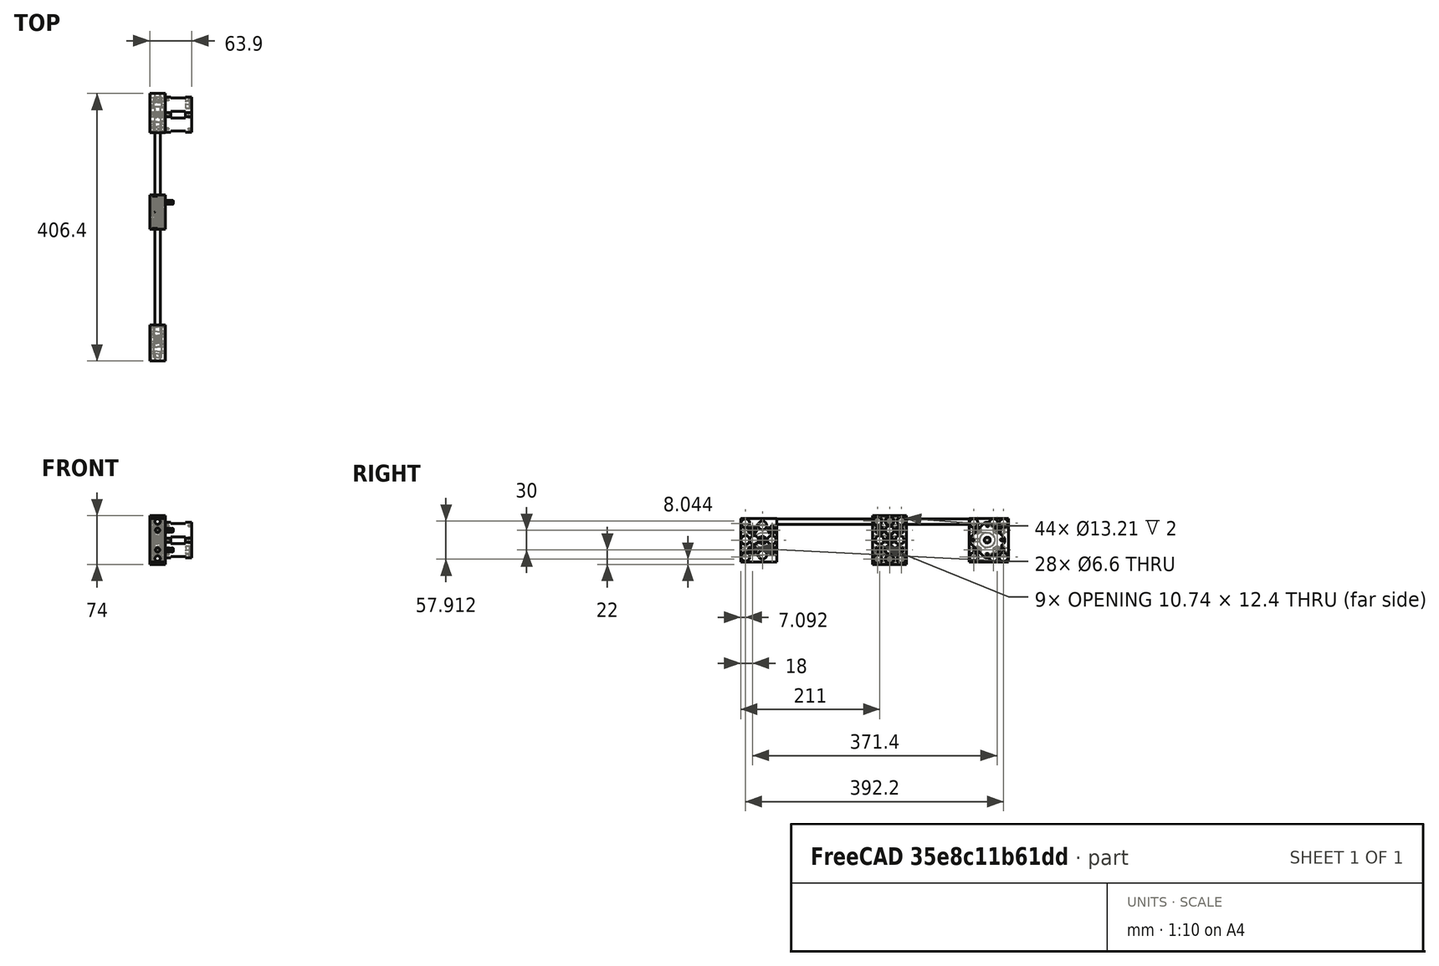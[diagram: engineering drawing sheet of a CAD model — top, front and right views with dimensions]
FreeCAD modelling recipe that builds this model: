
FCSTD DOCUMENT  (FreeCAD 0.16R6707 (Git))
Label: D3D Left Y Axis Simple
License: CreativeCommons Attribution
LicenseURL: http://creativecommons.org/licenses/by/4.0/
objects: Part::FeaturePython×7, Part::Feature×7, App::FeaturePython×4, Part::Mirroring×3, Part::MultiFuse×3, Part::Cylinder×1, App::DocumentObjectGroup×1
note: 21 computed .brp shape members not serialized (recipe doc carries the construction recipe); baked Part::Feature solids carry a one-line shape summary decoded from their .brp

FEATURE [Part::FeaturePython] Universal_axis_idler_side_01  # a2plus imported part (geometry in sourceFile) (typed FeaturePython)
  Placement = pos=(0,0,0) rot=(0.57735,0.57735,0.57735;2.0944rad)
  fixedPosition = true
  sourceFile = <userpath>/Downloads/Freecad/D3D Printer/Universal_axis_idler_side.fcstd
  timeLastImport = 1.48765e+09
  updateColors = true
FEATURE [Part::Mirroring] Part__Mirroring  label="Universal_axis_idler_side_01 (Mirror #1)"
  Base = (0,0,0)
  Normal = (1,0,0)
  Source = -> Universal_axis_idler_side_01
FEATURE [Part::MultiFuse] Fusion  label="Y1 Universal Axis Idler"
  Placement = pos=(12,33,33) rot=(0,0,1;0rad)
  Shapes = -> [Part__Mirroring,Universal_axis_idler_side_01]
FEATURE [Part::Cylinder] Cylinder  label="Rod"
  Angle = 360
  Height = 406.4
  Placement = pos=(12,9.155e-07,4.99999) rot=(0,0.707107,0.707107;3.14159rad)
  Radius = 3.96875
FEATURE [Part::FeaturePython] Clone006  label="Clone of Rod"  # Draft clone (typed FeaturePython)
  Objects = -> [Cylinder]
  Placement = pos=(11.9844,9.155e-07,61) rot=(-1,0,0;1.5708rad)
  Scale = (1,1,1)
FEATURE [Part::FeaturePython] Universal_axis_motor_side_01  # a2plus imported part (geometry in sourceFile) (typed FeaturePython)
  fixedPosition = false
  sourceFile = <userpath>/Downloads/Freecad/D3D Printer/Universal_axis_motor_side.fcstd
  timeLastImport = 1.48765e+09
  updateColors = true
FEATURE [Part::Mirroring] Part__Mirroring003  label="Universal_axis_motor_side_01 (Mirror #3)"
  Base = (0,0,0)
  Normal = (0,0,1)
  Source = -> Universal_axis_motor_side_01
FEATURE [Part::MultiFuse] Fusion005  label="Y1 Universal Axis Motor"
  Placement = pos=(12,374.4,33) rot=(0.57735,-0.57735,-0.57735;2.0944rad)
  Shapes = -> [Part__Mirroring003,Universal_axis_motor_side_01]
FEATURE [App::FeaturePython] planeConstraint01  label="Rods"  # a2plus constraint (typed FeaturePython)
  Object1 = Fusion005
  Object2 = Cylinder
  SubElement1 = Face3
  SubElement2 = Face2
  Type = plane
  directionConstraint = 0
  offset = 0
FEATURE [App::FeaturePython] planeConstraint02  label="Rods / Axis Motor "  # a2plus constraint (typed FeaturePython)
  Object1 = Fusion005
  Object2 = Clone006
  SubElement1 = Face42
  SubElement2 = Face2
  Type = plane
  directionConstraint = 0
  offset = 0
FEATURE [App::FeaturePython] planeConstraint03  label="Rods / Axis Idler"  # a2plus constraint (typed FeaturePython)
  Object1 = Fusion
  Object2 = Cylinder
  SubElement1 = Face3
  SubElement2 = Face3
  Type = plane
  directionConstraint = 1
  offset = 0
FEATURE [Part::FeaturePython] carriage_8mm_rods_01  # a2plus imported part (geometry in sourceFile) (typed FeaturePython)
  Placement = pos=(12.5,0,0) rot=(0,0,1;0rad)
  fixedPosition = false
  sourceFile = <userpath>/Downloads/Freecad/D3D Printer/Mess Stuff/axis_8mm STL + FCSTD/carriage_8mm_rods.FCStd
  timeLastImport = 1.48802e+09
  updateColors = true
FEATURE [Part::Mirroring] Part__Mirroring004  label="carriage_8mm_rods_01 (Mirror #3)"
  Base = (0,0,0)
  Normal = (0,0,1)
  Source = -> carriage_8mm_rods_01
FEATURE [Part::Feature] Part__Feature001  label="Pulley"
  Placement = pos=(20,374.4,33) rot=(0.678598,-0.678598,0.281085;2.59356rad)
  shape: bbox 11 x 12.62 x 12.62 mm, 94 faces (baked)
FEATURE [Part::Feature] Part__Feature002  label="MK8"
  Placement = pos=(16.9019,376.706,30.8284) rot=(1,0,0;2.35619rad)
  shape: bbox 3 x 3.394 x 3.394 mm, 13 faces (baked)
FEATURE [App::DocumentObjectGroup] Group  label="nuts bolts"
FEATURE [Part::Feature] Part__Feature003  label="ball_bearing"
  Placement = pos=(14,33,33) rot=(0,-1,0;1.5708rad)
  shape: bbox 8 x 13.6 x 13.6 mm, 82 faces (baked)
FEATURE [Part::Feature] Part__Feature004  label="lmuu 8mm bearing"
  Placement = pos=(0,-28,0) rot=(0,0,1;1.5708rad)
  shape: bbox 24 x 15 x 15 mm, 38 faces (baked)
FEATURE [Part::FeaturePython] Clone  label="lmuu 8mm bearing001"  # Draft clone (typed FeaturePython)
  Objects = -> [Part__Feature004]
  Placement = pos=(25,-28,0) rot=(0,0,1;1.5708rad)
  Scale = (1,1,1)
FEATURE [Part::FeaturePython] Clone007  label="lmuu 8mm bearing002"  # Draft clone (typed FeaturePython)
  Objects = -> [Part__Feature004]
  Placement = pos=(0,28,0) rot=(0,0,1;1.5708rad)
  Scale = (1,1,1)
FEATURE [Part::FeaturePython] Clone008  label="lmuu 8mm bearing003"  # Draft clone (typed FeaturePython)
  Objects = -> [Clone007]
  Placement = pos=(25,28,0) rot=(0,0,1;1.5708rad)
  Scale = (1,1,1)
FEATURE [Part::MultiFuse] Fusion006  label="Y1 Universal Axis Carriage"
  Placement = pos=(11.9844,238.5,33) rot=(0.57735,-0.57735,-0.57735;2.0944rad)
  Shapes = -> [Part__Mirroring004,carriage_8mm_rods_01,Part__Feature004,Clone,Clone007,Clone008]
FEATURE [Part::Feature] Part__Feature007  label="M6x30 001"
  Placement = pos=(35.9844,241,18) rot=(0,1,0;1.5708rad)
  shape: bbox 36.21 x 10 x 10 mm, 148 faces (baked)
FEATURE [Part::Feature] Part__Feature  label="Nema 17 Step Motor"
  Placement = pos=(63.878,374.4,33) rot=(0.678598,-0.281085,-0.678598;2.59356rad)
  shape: bbox 61.88 x 53.46 x 53.46 mm, 81 faces (baked)
FEATURE [App::FeaturePython] circularEdgeConstraint01  # a2plus constraint (typed FeaturePython)
  Object1 = Fusion005
  Object2 = Part__Feature
  SubElement1 = Edge21
  SubElement2 = Edge134
  Type = circularEdge
  directionConstraint = 0
  lockRotation = false
  offset = 0
FEATURE [Part::Feature] Part__Feature006  label="M6x30"
  Placement = pos=(35.9844,241.06,47.9257) rot=(0,1,0;1.5708rad)
  shape: bbox 36.21 x 10 x 10 mm, 148 faces (baked)
